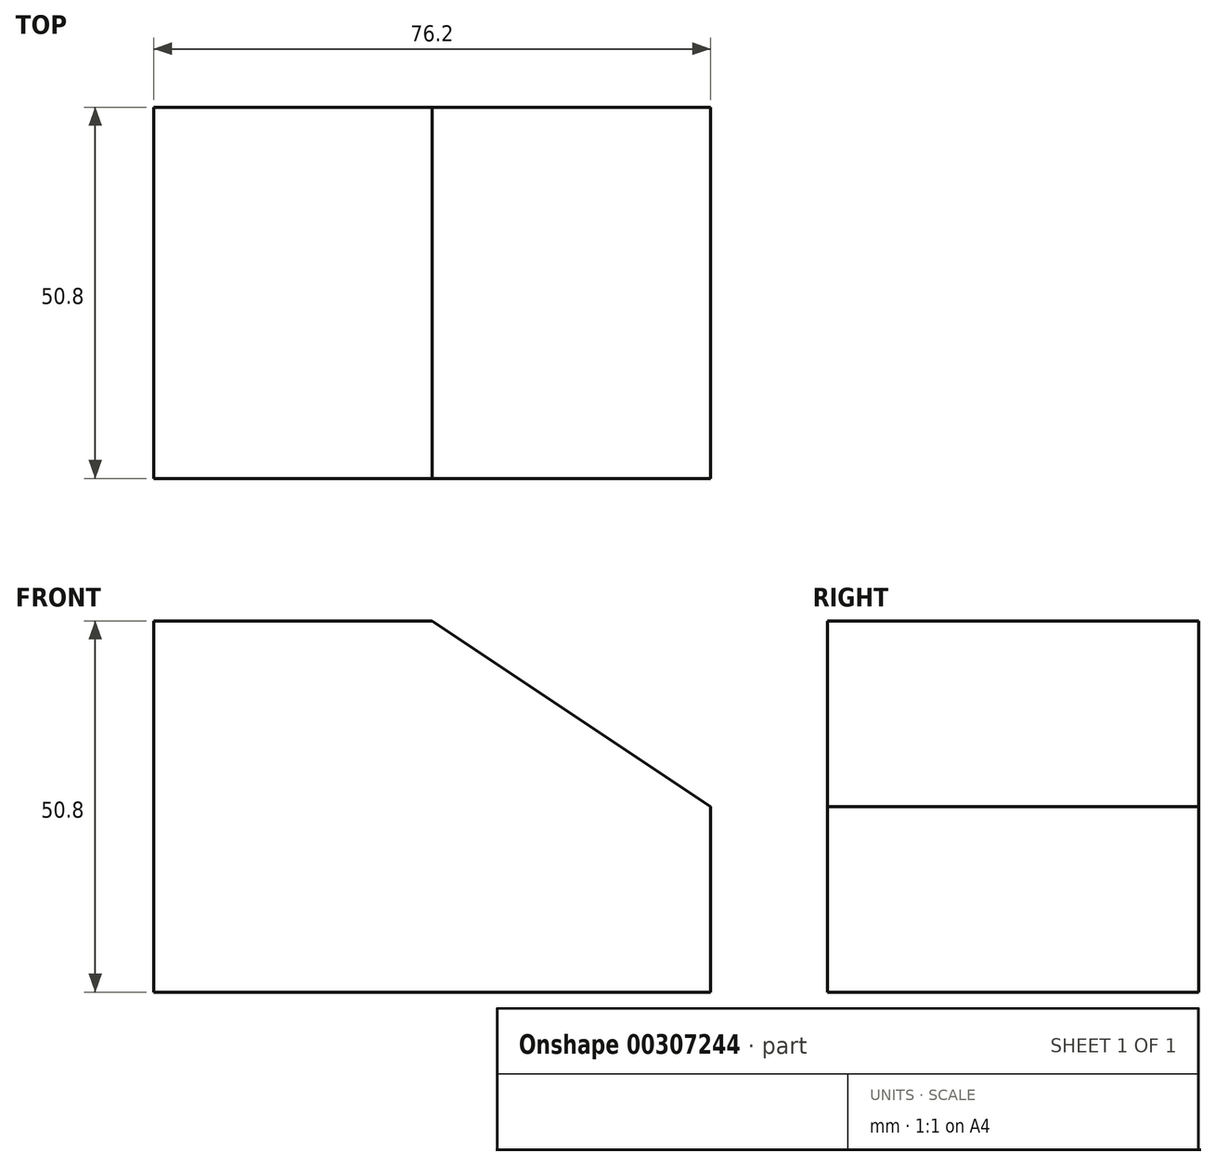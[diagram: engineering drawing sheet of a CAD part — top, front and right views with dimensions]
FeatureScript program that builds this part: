
annotation { "Feature Type Name" : "Feature", "Feature Type Description" : "" }
export const myFeature = defineFeature(function(context is Context, id is Id, definition is map)
    precondition{}
    {
        {
            var Q0;
            Q0=qCreatedBy(makeId("Front.planeOp"),FACE);
            var sketch = newSketch(context, id + "F0", { "sketchPlane" : qUnion([Q0])});
            skLineSegment(sketch, "E0", {"start": v(45.96, -24.26) * mm, "end": v(-30.24, -24.26) * mm});
            skLineSegment(sketch, "E1", {"start": v(-30.24, -24.26) * mm, "end": v(-30.24, 26.54) * mm});
            skLineSegment(sketch, "E2", {"start": v(-30.24, 26.54) * mm, "end": v(7.86, 26.54) * mm});
            skLineSegment(sketch, "E3", {"start": v(45.96, -24.26) * mm, "end": v(45.96, 1.14) * mm});
            skLineSegment(sketch, "E4", {"start": v(7.86, 26.54) * mm, "end": v(45.96, 1.14) * mm});
            skSolve(sketch);
        }
        {
            var Q0;
            Q0=makeQuery(id+"F0.imprint","IMPRINT",FACE,{"disambiguationData":[TD([[makeQuery(id+"F0.imprint","IMPRINT",EDGE,{"derivedFrom":sQuery(id+"F0.wireOp",EDGE,"E0")}),-1.0]])]});
            extrude(context, id + "F1", {"entities" : qUnion([Q0]), "depth" : 50.8 * mm});
        }
    });
